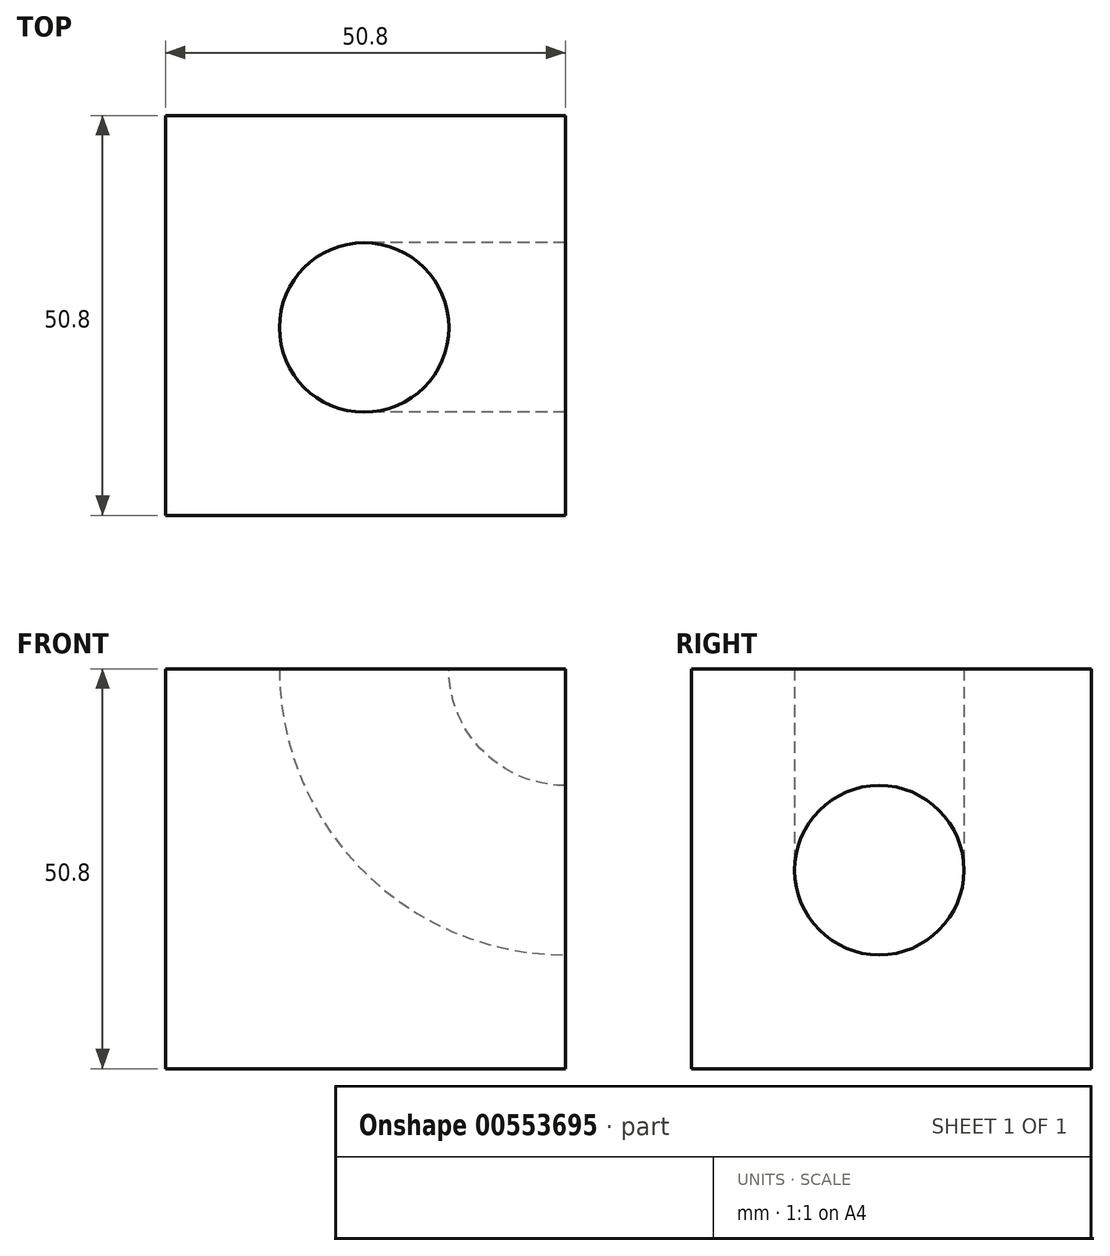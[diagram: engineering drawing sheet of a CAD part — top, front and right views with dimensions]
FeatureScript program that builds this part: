
annotation { "Feature Type Name" : "Feature", "Feature Type Description" : "" }
export const myFeature = defineFeature(function(context is Context, id is Id, definition is map)
    precondition{}
    {
        {
            var Q0;
            Q0=qCreatedBy(makeId("Top.planeOp"),FACE);
            var sketch = newSketch(context, id + "F0", { "sketchPlane" : qUnion([Q0])});
            skLineSegment(sketch, "E0.bottom", {"start": v(0, 0) * mm, "end": v(50.8, 0) * mm});
            skLineSegment(sketch, "E0.top", {"start": v(0, 50.8) * mm, "end": v(50.8, 50.8) * mm});
            skLineSegment(sketch, "E0.left", {"start": v(0, 0) * mm, "end": v(0, 50.8) * mm});
            skLineSegment(sketch, "E0.right", {"start": v(50.8, 0) * mm, "end": v(50.8, 50.8) * mm});
            skSolve(sketch);
        }
        {
            var Q0;
            Q0=makeQuery(id+"F0.imprint","IMPRINT",FACE,{"disambiguationData":[TD([[makeQuery(id+"F0.imprint","IMPRINT",EDGE,{"derivedFrom":sQuery(id+"F0.wireOp",EDGE,"E0.bottom")}),1.0]])]});
            extrude(context, id + "F1", {"entities" : qUnion([Q0]), "depth" : 50.8 * mm, "offsetDistance" : 25.4 * mm});
        }
        {
            var Q0;
            Q0=makeQuery(id+"F1.opExtrude","CAP_FACE",FACE,{"disambiguationData":[OSD([sQuery(id+"F0.wireOp",EDGE,"E0.bottom"),sQuery(id+"F0.wireOp",EDGE,"E0.top"),sQuery(id+"F0.wireOp",EDGE,"E0.left"),sQuery(id+"F0.wireOp",EDGE,"E0.right")])],"isStart":false});
            var sketch = newSketch(context, id + "F2", { "sketchPlane" : qUnion([Q0])});
            skCircle(sketch, "E1", {"center": v(25.21, 23.85) * mm, "radius": 10.76 * mm});
            skSolve(sketch);
        }
        {
            var Q0;
            Q0=makeQuery(id+"F2.imprint","IMPRINT",FACE,{"disambiguationData":[TD([[makeQuery(id+"F2.imprint","IMPRINT",EDGE,{"derivedFrom":sQuery(id+"F2.wireOp",EDGE,"E1")}),1.0]])]});
            var Q1;
            Q1=makeQuery(id+"F1.opExtrude","CAP_EDGE",EDGE,{"disambiguationData":[OSD([sQuery(id+"F0.wireOp",EDGE,"E0.right")])],"isStart":false});
            revolve(context, id + "F3", {"operationType" : NewBodyOperationType.REMOVE, "entities" : qUnion([Q0]), "axis" : qUnion([Q1]), "revolveType" : RevolveType.FULL, "oppositeDirection" : true});
        }
    });
